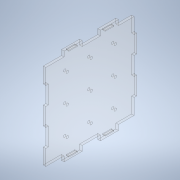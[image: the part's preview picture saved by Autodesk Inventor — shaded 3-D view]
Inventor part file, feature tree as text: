
AUTODESK INVENTOR PART (.ipt)
format: ipt  version: 2021 (Build 250183000, 183)  size: 194,560 bytes
history: native  units: mm
features: sketch x10, hole x9, extrude x1
ambient origin geometry x8: Origin, YZ Plane, XZ Plane, XY Plane, X Axis, Y Axis, Z Axis, Center Point
bodies: Solid1 (feature_tree)
feature tree (20):
  extrude  "Extrusion1"  Depth=3.0mm
  hole  "Hole2"  [1 undecoded]
  hole  "Hole3"  [1 undecoded]
  hole  "Hole4"  [1 undecoded]
  hole  "Hole5"  [1 undecoded]
  hole  "Hole6"  [1 undecoded]
  hole  "Hole7"  [1 undecoded]
  hole  "Hole8"  [1 undecoded]
  hole  "Hole9"  [1 undecoded]
  hole  "Hole10"  [1 undecoded]
  sketch  "Sketch1"  dims[d4=3.0mm d5=0.0mm d22=3.0mm]
  sketch  "Sketch3"  dims[d23=3.0mm d24=6.0mm d25=4.0mm d26=2.0mm d27=90.0deg d28=8.0mm d29=20.594885mm d30=3.0mm]
  sketch  "Sketch4"  dims[d31=3.0mm d32=6.0mm d33=4.0mm d34=2.0mm d35=90.0deg d36=8.0mm d37=20.594885mm d38=3.0mm]
  sketch  "Sketch5"  dims[d39=3.0mm d40=6.0mm d41=4.0mm d42=2.0mm d43=90.0deg d44=8.0mm d45=20.594885mm d46=3.0mm]
  sketch  "Sketch6"  dims[d47=3.0mm d48=6.0mm d49=4.0mm d50=2.0mm d51=90.0deg d52=8.0mm d53=20.594885mm d54=3.0mm]
  sketch  "Sketch7"  dims[d55=3.0mm d56=6.0mm d57=4.0mm d58=2.0mm d59=90.0deg d60=8.0mm d61=20.594885mm d62=3.0mm]
  sketch  "Sketch8"  dims[d63=3.0mm d64=6.0mm d65=4.0mm d66=2.0mm d67=90.0deg d68=8.0mm d69=20.594885mm d70=3.0mm]
  sketch  "Sketch9"  dims[d71=3.0mm d72=6.0mm d73=4.0mm d74=2.0mm d75=90.0deg d76=8.0mm d77=20.594885mm d78=3.0mm]
  sketch  "Sketch10"  dims[d79=3.0mm d80=6.0mm d81=4.0mm d82=2.0mm d83=90.0deg d84=8.0mm d85=20.594885mm d86=3.0mm]
  sketch  "Sketch11"  dims[d87=3.0mm d88=6.0mm d89=4.0mm d90=2.0mm d91=90.0deg d92=8.0mm d93=20.594885mm d94=1.0mm d95=10.0mm d96=1.0mm d97=10.0mm d98=10.0mm d99=1.0mm d100=10.0mm]
note: 9 required parameter values undecoded (feature->parameter linkage not recoverable at this tier; creation-order binding heuristic only, values carry confidence <= 0.55)
